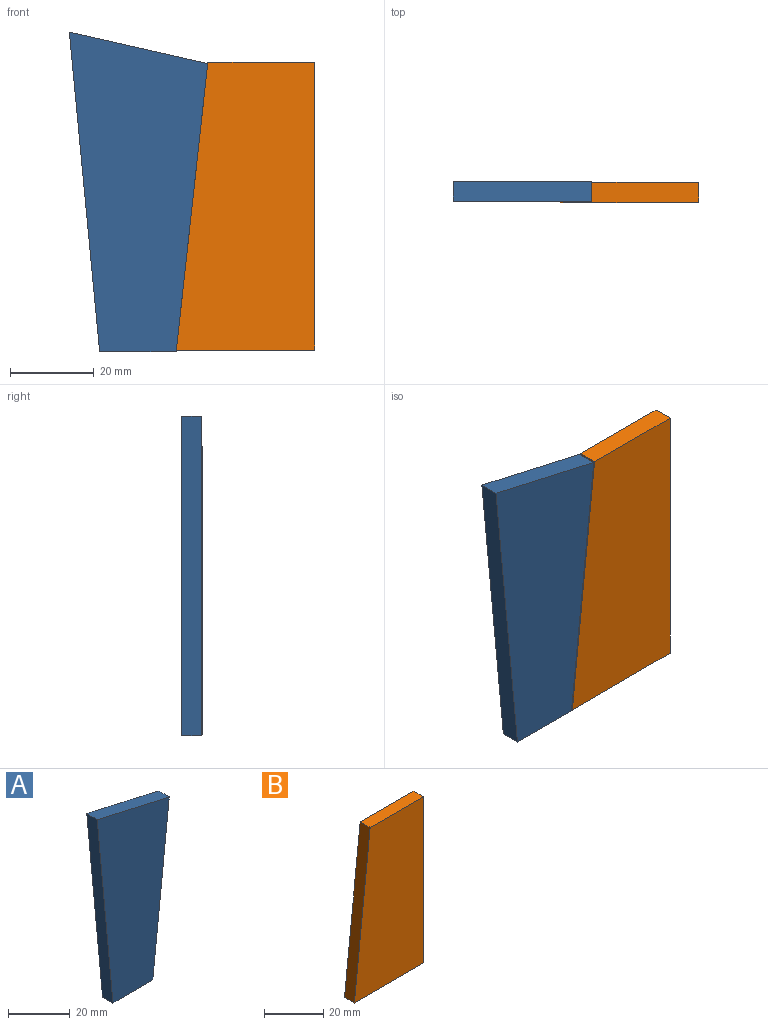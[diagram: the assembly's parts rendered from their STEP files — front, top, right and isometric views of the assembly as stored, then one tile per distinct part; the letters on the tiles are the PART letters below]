
ASSEMBLY  parts=2 mates=1
PART A: 6 faces, bbox 33.1x4.8x76.5 mm
  f0: plane 76.47x7.23mm, normal (-1,0,-0.09), area 365.8mm2, adj f1,f3,f4,f5
  f1: plane 18.31x4.76mm, normal (0,0,-1), area 87.2mm2, adj f0,f2,f4,f5
  f2: plane 68.94x7.53mm, normal (0.99,0,-0.11), area 330.3mm2, adj f1,f3,f4,f5
  f3: plane 33.07x7.53mm, normal (0.22,0,0.98), area 161.5mm2, adj f0,f2,f4,f5
  f4: plane 76.47x33.07mm, normal (0,-1,0), area 1868mm2, adj f0,f1,f2,f3
  f5: plane 76.47x33.07mm, normal (0,1,0), area 1868mm2, adj f0,f1,f2,f3
PART B: 6 faces, bbox 33.1x4.8x68.9 mm
  f0: plane 25.54x4.76mm, normal (0,0,1), area 121.6mm2, adj f1,f3,f4,f5
  f1: plane 68.94x7.53mm, normal (-0.99,0,0.11), area 330.3mm2, adj f0,f2,f4,f5
  f2: plane 33.07x4.76mm, normal (0,0,-1), area 157.5mm2, adj f1,f3,f4,f5
  f3: plane 68.8x4.76mm, normal (1,0,0), area 327.6mm2, adj f0,f2,f4,f5
  f4: plane 68.94x33.07mm, normal (0,-1,0), area 2017.7mm2, adj f0,f1,f2,f3
  f5: plane 68.94x33.07mm, normal (0,1,0), area 2017.7mm2, adj f0,f1,f2,f3
PLACE A t=(-17.87,-10.92,4.82)mm fixed
PLACE B t=(-20.2,-11.15,5.13)mm
MATE planar A.f2 <-> B.f1  axis (0.99,0,-0.11) through (-45.62,-15.68,-31.27)mm
